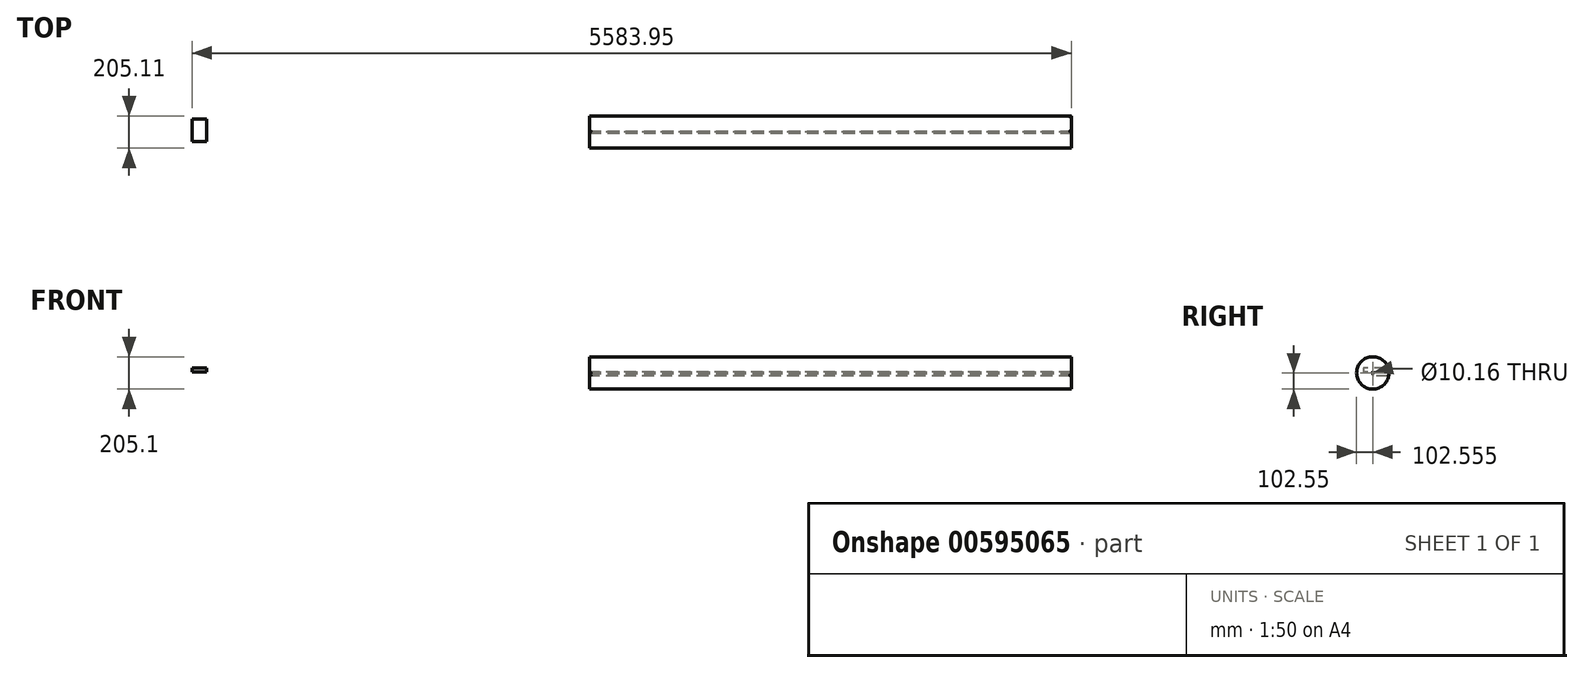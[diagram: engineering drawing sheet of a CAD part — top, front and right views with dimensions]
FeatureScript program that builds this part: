
annotation { "Feature Type Name" : "Feature", "Feature Type Description" : "" }
export const myFeature = defineFeature(function(context is Context, id is Id, definition is map)
    precondition{}
    {
        {
            var Q0;
            Q0=qCreatedBy(makeId("Top.planeOp"),FACE);
            var sketch = newSketch(context, id + "F0", { "sketchPlane" : qUnion([Q0])});
            skLineSegment(sketch, "E0.bottom", {"start": v(-28.88, 42) * mm, "end": v(61.75, 42) * mm});
            skLineSegment(sketch, "E0.top", {"start": v(-28.88, -101.03) * mm, "end": v(61.75, -101.03) * mm});
            skLineSegment(sketch, "E0.left", {"start": v(-28.88, 42) * mm, "end": v(-28.88, -101.03) * mm});
            skLineSegment(sketch, "E0.right", {"start": v(61.75, 42) * mm, "end": v(61.75, -101.03) * mm});
            skSolve(sketch);
        }
        {
            var Q0;
            Q0=makeQuery(id+"F0.imprint","IMPRINT",FACE,{"disambiguationData":[TD([[makeQuery(id+"F0.imprint","IMPRINT",EDGE,{"derivedFrom":sQuery(id+"F0.wireOp",EDGE,"E0.bottom")}),-1.0]])]});
            extrude(context, id + "F1", {"entities" : qUnion([Q0]), "depth" : 25.4 * mm, "offsetDistance" : 25.4 * mm});
        }
        {
            var Q0;
            Q0=makeQuery(id+"F1.opExtrude","CAP_FACE",FACE,{"disambiguationData":[OSD([sQuery(id+"F0.wireOp",EDGE,"E0.bottom"),sQuery(id+"F0.wireOp",EDGE,"E0.top"),sQuery(id+"F0.wireOp",EDGE,"E0.left"),sQuery(id+"F0.wireOp",EDGE,"E0.right")])],"isStart":true});
            var sketch = newSketch(context, id + "F2", { "sketchPlane" : qUnion([Q0])});
            skLineSegment(sketch, "E1.bottom", {"start": v(5555.07, -60.82) * mm, "end": v(2494.48, -60.82) * mm});
            skLineSegment(sketch, "E1.top", {"start": v(5555.07, 41.6) * mm, "end": v(2494.48, 41.6) * mm});
            skLineSegment(sketch, "E1.left", {"start": v(5555.07, -60.82) * mm, "end": v(5555.07, 41.6) * mm});
            skLineSegment(sketch, "E1.right", {"start": v(2494.48, -60.82) * mm, "end": v(2494.48, 41.6) * mm});
            skSolve(sketch);
        }
        {
            var Q0;
            Q0 = qSketchRegion(id + "F2", true);
            extrude(context, id + "F3", {"entities" : qUnion([Q0]), "depth" : 25.4 * mm, "offsetDistance" : 25.4 * mm});
        }
        {
            var Q0;
            Q0=makeQuery(id+"F3.opExtrude","CAP_EDGE",EDGE,{"disambiguationData":[OSD([sQuery(id+"F2.wireOp",EDGE,"E1.bottom")])],"isStart":false});
            fillet(context, id + "F4", {"entities" : qUnion([Q0]), "radius" : 5.08 * mm, "tangentPropagation" : true, "allowEdgeOverflow" : false});
        }
        {
            var Q0;
            Q0=makeQuery(id+"F3.opExtrude","CAP_FACE",FACE,{"disambiguationData":[OSD([sQuery(id+"F2.wireOp",EDGE,"E1.bottom"),sQuery(id+"F2.wireOp",EDGE,"E1.top"),sQuery(id+"F2.wireOp",EDGE,"E1.left"),sQuery(id+"F2.wireOp",EDGE,"E1.right")])],"isStart":true});
            var Q1;
            Q1=makeQuery(id+"F3.opExtrude","SWEPT_FACE",FACE,{"disambiguationData":[OSD([sQuery(id+"F2.wireOp",EDGE,"E1.top")])]});
            var Q2;
            Q2=makeQuery(id+"F3.opExtrude","CAP_EDGE",EDGE,{"disambiguationData":[OSD([sQuery(id+"F2.wireOp",EDGE,"E1.bottom")])],"isStart":true});
            var Q3;
            Q3=makeQuery(id+"F3.opExtrude","CAP_EDGE",EDGE,{"disambiguationData":[OSD([sQuery(id+"F2.wireOp",EDGE,"E1.top")])],"isStart":true});
            var Q4;
            Q4=makeQuery(id+"F4.opFillet","BLEND_FACE",FACE,{"disambiguationData":[OSD([sQuery(id+"F2.wireOp",EDGE,"E1.bottom")])]});
            var Q5;
            Q5=makeQuery(id+"F3.opExtrude","SWEPT_FACE",FACE,{"disambiguationData":[OSD([sQuery(id+"F2.wireOp",EDGE,"E1.bottom")])]});
            var Q6;
            Q6=makeQuery(id+"F3.opExtrude","CAP_EDGE",EDGE,{"disambiguationData":[OSD([sQuery(id+"F2.wireOp",EDGE,"E1.top")])],"isStart":false});
            var Q7;
            {var subQ0=sQuery(id+"F2.wireOp",EDGE,"E1.bottom");Q7=makeQuery(id+"F4.opFillet","BLEND_EDGE",EDGE,{"blendedFrom":[makeQuery(id+"F3.opExtrude","CAP_EDGE",EDGE,{"disambiguationData":[OSD([subQ0])],"isStart":false}),makeQuery(id+"F3.opExtrude","SWEPT_FACE",FACE,{"disambiguationData":[OSD([subQ0])]})],"blendedInto":[makeQuery(id+"F3.opExtrude","SWEPT_FACE",FACE,{"disambiguationData":[OSD([subQ0])]})]});}
            var Q8;
            Q8=makeQuery(id+"F3.opExtrude","CAP_FACE",FACE,{"disambiguationData":[OSD([sQuery(id+"F2.wireOp",EDGE,"E1.bottom"),sQuery(id+"F2.wireOp",EDGE,"E1.top"),sQuery(id+"F2.wireOp",EDGE,"E1.left"),sQuery(id+"F2.wireOp",EDGE,"E1.right")])],"isStart":false});
            var Q9;
            {var subQ0=sQuery(id+"F2.wireOp",EDGE,"E1.bottom");Q9=makeQuery(id+"F4.opFillet","BLEND_EDGE",EDGE,{"blendedFrom":[makeQuery(id+"F3.opExtrude","CAP_EDGE",EDGE,{"disambiguationData":[OSD([subQ0])],"isStart":false}),makeQuery(id+"F3.opExtrude","CAP_FACE",FACE,{"disambiguationData":[OSD([subQ0,sQuery(id+"F2.wireOp",EDGE,"E1.top"),sQuery(id+"F2.wireOp",EDGE,"E1.left"),sQuery(id+"F2.wireOp",EDGE,"E1.right")])],"isStart":false})],"blendedInto":[makeQuery(id+"F3.opExtrude","CAP_FACE",FACE,{"disambiguationData":[OSD([subQ0,sQuery(id+"F2.wireOp",EDGE,"E1.top"),sQuery(id+"F2.wireOp",EDGE,"E1.left"),sQuery(id+"F2.wireOp",EDGE,"E1.right")])],"isStart":false})]});}
            fillet(context, id + "F5", {"entities" : qUnion([Q0, Q1, Q2, Q3, Q4, Q5, Q6, Q7, Q8, Q9]), "radius" : 5.08 * mm, "tangentPropagation" : true, "allowEdgeOverflow" : false});
        }
        {
            var Q0;
            Q0 = qSketchRegion(id + "F2", true);
            var Q1;
            {var subQ0=sQuery(id+"F2.wireOp",EDGE,"E1.top");Q1=makeQuery(id+"F5.opFillet","BLEND_EDGE",EDGE,{"blendedFrom":[makeQuery(id+"F3.opExtrude","CAP_EDGE",EDGE,{"disambiguationData":[OSD([subQ0])],"isStart":true}),makeQuery(id+"F3.opExtrude","SWEPT_FACE",FACE,{"disambiguationData":[OSD([subQ0])]})],"blendedInto":[makeQuery(id+"F3.opExtrude","SWEPT_FACE",FACE,{"disambiguationData":[OSD([subQ0])]})]});}
            revolve(context, id + "F6", {"entities" : qUnion([Q0]), "axis" : qUnion([Q1]), "revolveType" : RevolveType.FULL});
        }
    });
